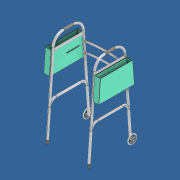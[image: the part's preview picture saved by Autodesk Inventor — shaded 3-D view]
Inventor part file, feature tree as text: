
AUTODESK INVENTOR PART (.ipt)
format: ipt  version: 2021 (Build 250183000, 183)  size: 1,015,296 bytes
history: native  units: in
note: dims shown in document units (in); Inventor stores cm internally (conversion verified against a paired STEP export)
features: extrude x4, sketch x4, plane x3, fillet x2, mirror x1, sweep x1
ambient origin geometry x8: Origin, YZ Plane, XZ Plane, XY Plane, X Axis, Y Axis, Z Axis, Center Point
bodies: Solid1 (feature_tree)
feature tree (15):
  plane  "Work Plane1"
  extrude  "Extrusion1"  Depth=0.2756in TaperAngle=0.0deg
  extrude  "Extrusion2"  Depth=0.3937in
  extrude  "Extrusion3"  Depth=10.2445in
  plane  "Work Plane2"
  fillet  "Fillet1"  [1 undecoded]
  mirror  "Mirror1"
  plane  "Work Plane3"
  extrude  "Extrusion4"  Depth=0.0394in TaperAngle=0.0deg
  fillet  "Fillet2"  Radius=0.1969in
  sketch  "Sketch1"  dims[d0=0.4375in d1=0.2756in d2=0.0in]
  sketch  "Sketch2"  dims[d6=0.3937in d7=0.3937in]
  sketch  "Sketch3"  dims[d8=10.2445in d9=10.2445in d10=180.0deg]
  sketch  "Sketch4"  dims[d11=180.0deg d12=2.3622in d13=0.0in d14=0.1969in d15=0.0in d16=-10.0in d17=0.0787in d18=31.0625in d21=0.1582in d22=0.3543in d23=0.1773in d24=0.3937in d25=0.1969in d26=0.4331in d27=0.2165in d28=0.4724in d29=0.2362in d30=0.5118in d31=0.2559in d32=0.5512in d33=0.5906in d34=0.2362in d35=0.2362in d36=0.2362in d37=0.2362in d38=0.2362in d39=0.2362in d40=0.2362in d41=0.2362in d43=0.5315in d44=0.5709in d45=0.6102in d46=0.6496in d47=0.689in d48=0.7283in d50=0.1378in d51=0.3543in d52=0.3937in d53=0.4331in d54=0.4724in d55=0.5118in d56=0.5512in d57=0.5906in d58=0.6299in d59=0.6693in d60=0.0394in d61=0.1181in d63=0.0394in d66=0.0394in d67=0.0394in d68=0.0394in d69=0.0394in d70=0.0394in d71=0.1181in d72=0.315in d73=0.0in d74=0.0787in d75=6.0236in d76=0.2953in d77=0.2756in d79=0.0394in d86=0.5485in d87=0.5085in d88=0.5847in d89=7.4606in]
  sweep  "Sweep5"
note: 1 required parameter value undecoded (feature->parameter linkage not recoverable at this tier; creation-order binding heuristic only, values carry confidence <= 0.55)
